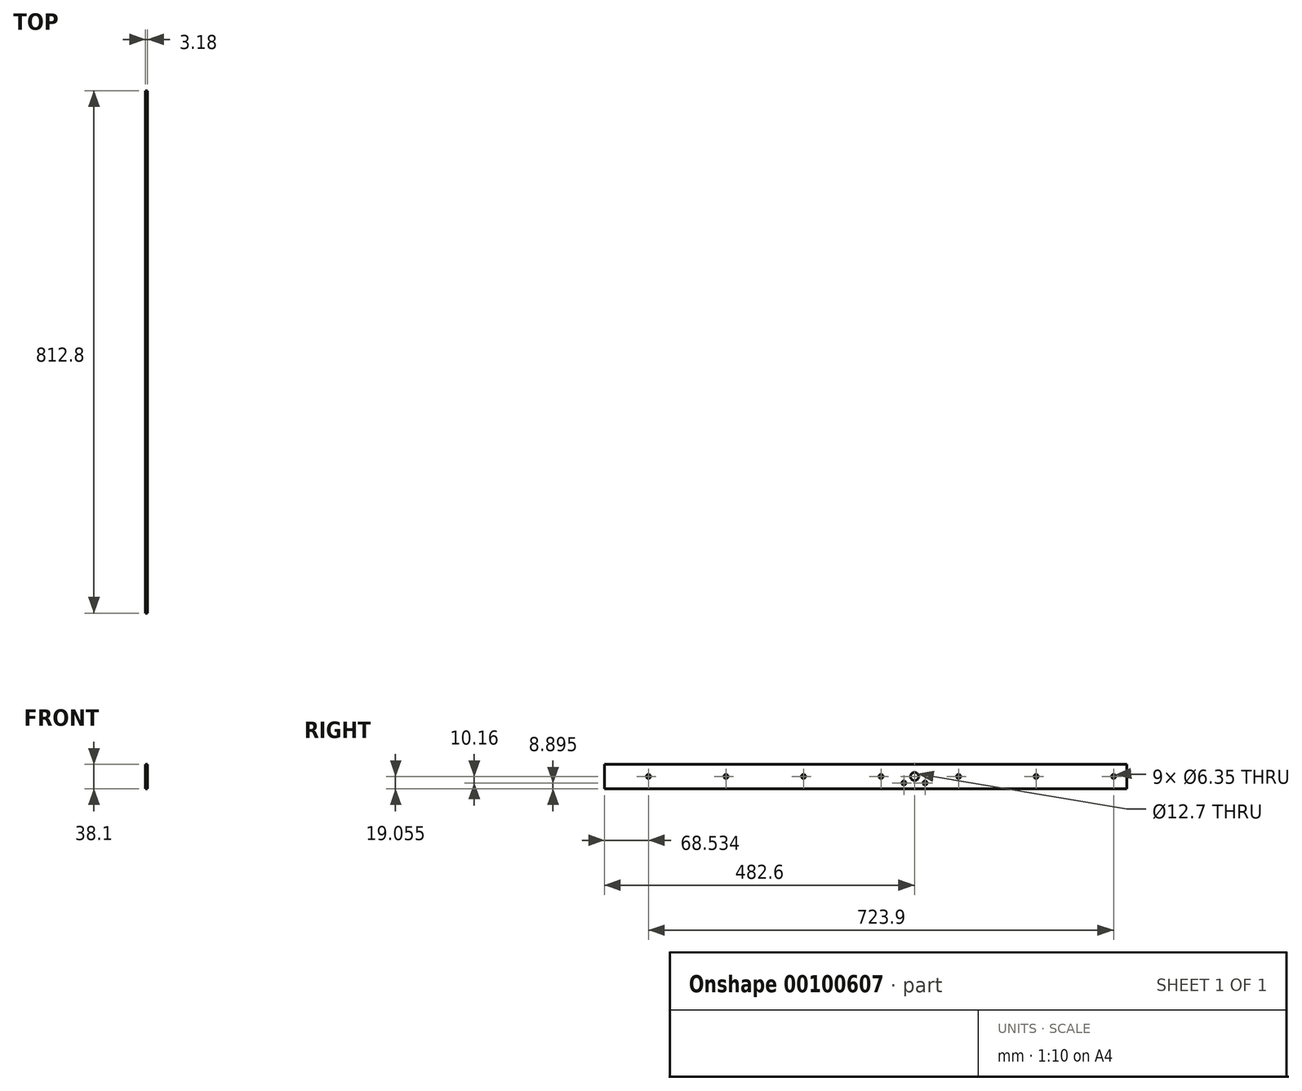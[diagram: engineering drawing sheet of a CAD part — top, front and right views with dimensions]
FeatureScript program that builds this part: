
annotation { "Feature Type Name" : "Feature", "Feature Type Description" : "" }
export const myFeature = defineFeature(function(context is Context, id is Id, definition is map)
    precondition{}
    {
        {
            var Q0;
            Q0=qCreatedBy(makeId("Front.planeOp"),FACE);
            var sketch = newSketch(context, id + "F0", { "sketchPlane" : qUnion([Q0])});
            skLineSegment(sketch, "E0", {"start": v(0, 0) * mm, "end": v(0, 34.92) * mm});
            skLineSegment(sketch, "E1", {"start": v(0, 34.92) * mm, "end": v(-3.18, 34.92) * mm});
            skLineSegment(sketch, "E2", {"start": v(-3.18, 34.92) * mm, "end": v(-3.17, -3.18) * mm});
            skLineSegment(sketch, "E3", {"start": v(-3.17, -3.18) * mm, "end": v(0, -3.18) * mm});
            skLineSegment(sketch, "E4", {"start": v(0, -3.18) * mm, "end": v(0, 0) * mm});
            skLineSegment(sketch, "E5", {"start": v(0, 0) * mm, "end": v(0, 0) * mm});
            skSolve(sketch);
        }
        {
            var Q0;
            Q0 = qSketchRegion(id + "F0", true);
            extrude(context, id + "F1", {"entities" : qUnion([Q0]), "depth" : 812.8 * mm});
        }
        {
            var Q0;
            Q0=makeQuery(id+"F1.opExtrude","SWEPT_FACE",FACE,{"disambiguationData":[OSD([sQuery(id+"F0.wireOp",EDGE,"E0")])]});
            var sketch = newSketch(context, id + "F2", { "sketchPlane" : qUnion([Q0])});
            skCircle(sketch, "E6", {"center": v(-330.2, 15.88) * mm, "radius": 6.35 * mm});
            skPoint(sketch, "E6.centerSnap0", {"position": v(0, 15.88) * mm});
            skCircle(sketch, "E7", {"center": v(-346.71, 5.71) * mm, "radius": 3.18 * mm});
            skLineSegment(sketch, "E8", {"start": v(-355.6, 34.92) * mm, "end": v(-355.6, 34.92) * mm});
            skLineSegment(sketch, "E9", {"start": v(-355.6, 34.92) * mm, "end": v(-304.8, 34.92) * mm, "construction": true});
            skLineSegment(sketch, "E10", {"start": v(-304.8, 34.92) * mm, "end": v(-304.8, 0) * mm, "construction": true});
            skLineSegment(sketch, "E11", {"start": v(-330.2, 34.92) * mm, "end": v(-330.2, 0) * mm, "construction": true});
            skCircle(sketch, "E12.MirrorC", {"center": v(-313.7, 5.71) * mm, "radius": 3.18 * mm});
            skSolve(sketch);
        }
        {
            var Q0;
            Q0 = qSketchRegion(id + "F2", true);
            extrude(context, id + "F3", {"entities" : qUnion([Q0]), "operationType" : NewBodyOperationType.REMOVE, "oppositeDirection" : true, "depth" : 25.4 * mm});
        }
        {
            var Q0;
            Q0=makeQuery(id+"F1.opExtrude","SWEPT_FACE",FACE,{"disambiguationData":[OSD([sQuery(id+"F0.wireOp",EDGE,"E0")])]});
            var sketch = newSketch(context, id + "F4", { "sketchPlane" : qUnion([Q0])});
            skCircle(sketch, "E13", {"center": v(-20.37, 15.87) * mm, "radius": 3.18 * mm});
            skPoint(sketch, "E13.centerSnap0", {"position": v(0, 15.87) * mm});
            skCircle(sketch, "E14.1.0.0", {"center": v(-141.02, 15.88) * mm, "radius": 3.18 * mm});
            skCircle(sketch, "E14.2.0.0", {"center": v(-261.67, 15.88) * mm, "radius": 3.18 * mm});
            skCircle(sketch, "E14.3.0.0", {"center": v(-382.32, 15.88) * mm, "radius": 3.18 * mm});
            skCircle(sketch, "E14.4.0.0", {"center": v(-502.97, 15.88) * mm, "radius": 3.18 * mm});
            skCircle(sketch, "E14.5.0.0", {"center": v(-623.62, 15.88) * mm, "radius": 3.18 * mm});
            skCircle(sketch, "E14.6.0.0", {"center": v(-744.27, 15.88) * mm, "radius": 3.18 * mm});
            skLineSegment(sketch, "E14.direction1", {"start": v(-20.37, 15.88) * mm, "end": v(-141.02, 15.88) * mm, "construction": true});
            skSolve(sketch);
        }
        {
            var Q0;
            Q0 = qSketchRegion(id + "F4", true);
            extrude(context, id + "F5", {"entities" : qUnion([Q0]), "operationType" : NewBodyOperationType.REMOVE, "oppositeDirection" : true, "depth" : 25.4 * mm});
        }
    });
